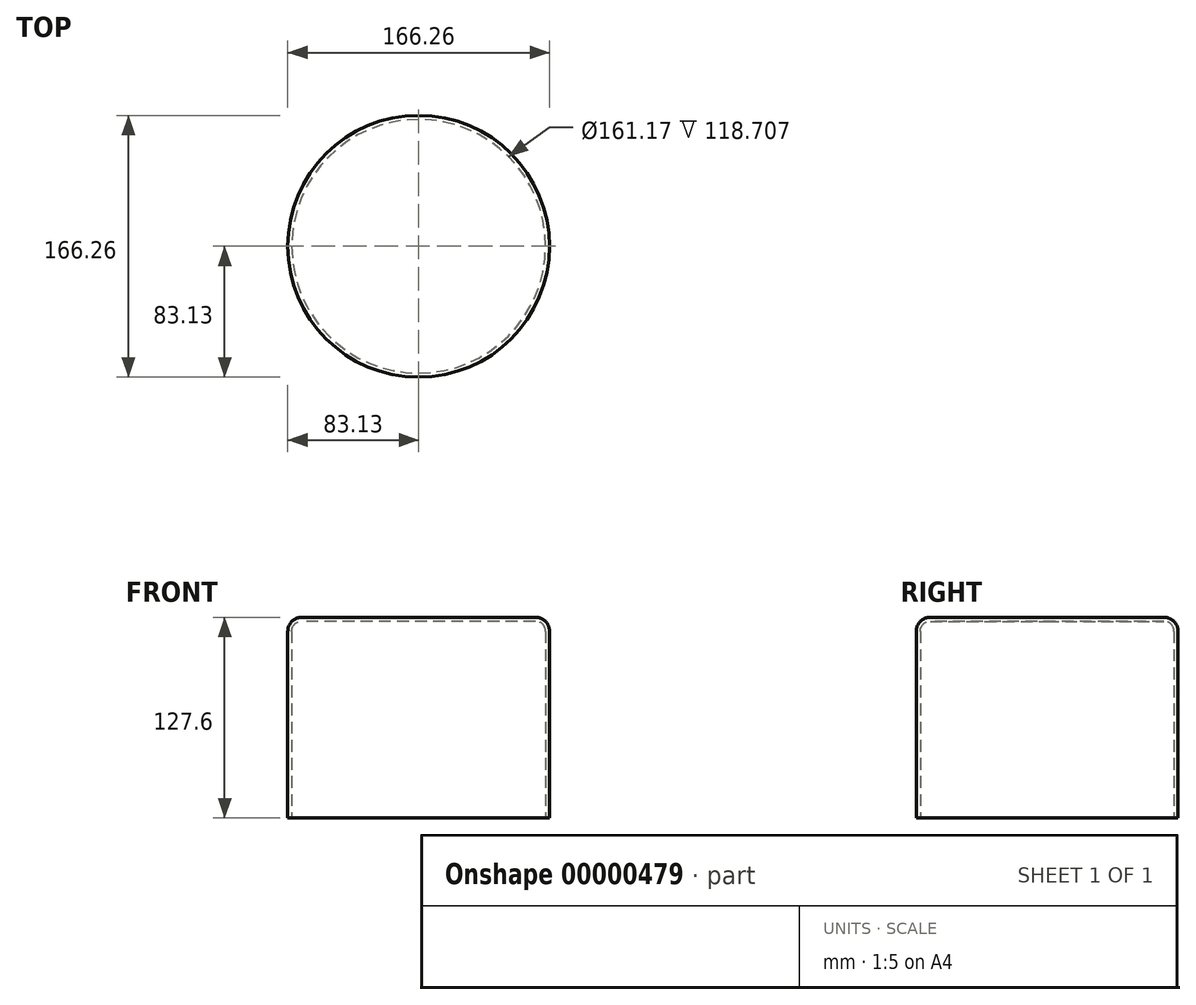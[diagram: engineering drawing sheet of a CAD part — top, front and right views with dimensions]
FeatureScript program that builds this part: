
annotation { "Feature Type Name" : "Feature", "Feature Type Description" : "" }
export const myFeature = defineFeature(function(context is Context, id is Id, definition is map)
    precondition{}
    {
        {
            var Q0;
            Q0 = qCreatedBy(makeId("Top.planeOp"), FACE);
            var sketch = newSketch(context, id + "F0", { "sketchPlane" : qUnion([Q0])});
            skCircle(sketch, "E0", {"center": v(0, 0) * mm, "radius": 83.13 * mm});
            skSolve(sketch);
        }
        {
            var Q0;
            Q0=makeQuery(id+"F0.imprint","IMPRINT",FACE,{"disambiguationData":[TD([[makeQuery(id+"F0.imprint","IMPRINT",EDGE,{"derivedFrom":sQuery(id+"F0.wireOp",EDGE,"E0")}),1.0]])]});
            extrude(context, id + "F1", {"entities" : qUnion([Q0]), "depth" : 127.6 * mm});
        }
        {
            var Q0;
            Q0=makeQuery(id+"F1.opExtrude","CAP_FACE",FACE,{"disambiguationData":[OSD([sQuery(id+"F0.wireOp",EDGE,"E0")])],"isStart":false});
            fillet(context, id + "F2", {"entities" : qUnion([Q0]), "radius" : 8.9 * mm, "tangentPropagation" : true, "allowEdgeOverflow" : false});
        }
        {
            var Q0;
            Q0=makeQuery(id+"F1.opExtrude","CAP_FACE",FACE,{"disambiguationData":[OSD([sQuery(id+"F0.wireOp",EDGE,"E0")])],"isStart":true});
            shell(context, id + "F3", {"entities" : qUnion([Q0]), "thickness" : 2.54 * mm});
        }
    });
